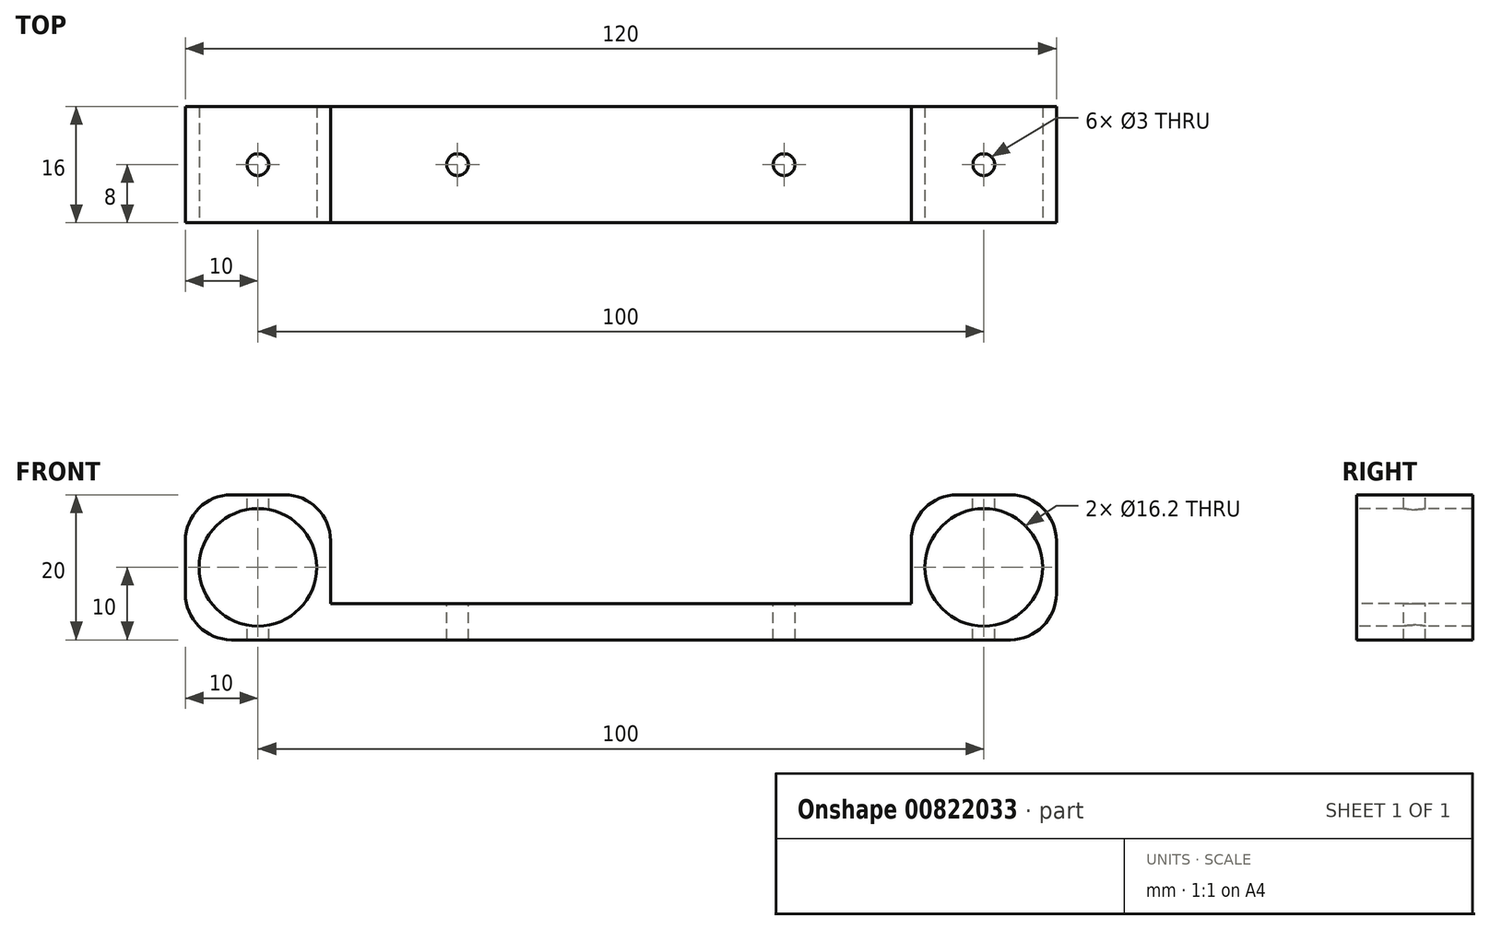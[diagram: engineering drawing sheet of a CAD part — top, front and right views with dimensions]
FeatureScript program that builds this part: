
annotation { "Feature Type Name" : "Feature", "Feature Type Description" : "" }
export const myFeature = defineFeature(function(context is Context, id is Id, definition is map)
    precondition{}
    {
        {
            var Q0;
            Q0=qCreatedBy(makeId("Top.planeOp"),FACE);
            var sketch = newSketch(context, id + "F0", { "sketchPlane" : qUnion([Q0])});
            skLineSegment(sketch, "E0.bottom", {"start": v(40, 8) * mm, "end": v(-40, 8) * mm});
            skLineSegment(sketch, "E0.top", {"start": v(40, -8) * mm, "end": v(-40, -8) * mm});
            skLineSegment(sketch, "E0.left", {"start": v(40, 8) * mm, "end": v(40, -8) * mm});
            skLineSegment(sketch, "E0.right", {"start": v(-40, 8) * mm, "end": v(-40, -8) * mm});
            skPoint(sketch, "E0.middle", {"position": v(0, 0) * mm});
            skLineSegment(sketch, "E1", {"start": v(40, -8) * mm, "end": v(40, 0) * mm});
            skLineSegment(sketch, "E2", {"start": v(-40, -8) * mm, "end": v(-40, 0) * mm});
            skSolve(sketch);
        }
        {
            var Q0;
            Q0=makeQuery(id+"F0.imprint","IMPRINT",FACE,{"disambiguationData":[TD([[makeQuery(id+"F0.imprint","IMPRINT",EDGE,{"derivedFrom":sQuery(id+"F0.wireOp",EDGE,"E0.bottom")}),1.0]])]});
            extrude(context, id + "F1", {"entities" : qUnion([Q0]), "depth" : 5 * mm, "offsetDistance" : 25.4 * mm});
        }
        {
            var Q0;
            Q0=makeQuery(id+"F1.opExtrude","SWEPT_FACE",FACE,{"disambiguationData":[OSD([sQuery(id+"F0.wireOp",EDGE,"E0.left"),sQuery(id+"F0.wireOp",EDGE,"E1")])]});
            var sketch = newSketch(context, id + "F2", { "sketchPlane" : qUnion([Q0])});
            skLineSegment(sketch, "E3.bottom", {"start": v(-8, 0) * mm, "end": v(8, 0) * mm});
            skLineSegment(sketch, "E3.right", {"start": v(8, 0) * mm, "end": v(8, -16) * mm});
            skLineSegment(sketch, "E4", {"start": v(-8, 0) * mm, "end": v(8, -16) * mm});
            skSolve(sketch);
        }
        {
            var Q0;
            Q0 = qSketchRegion(id + "F2", true);
            extrude(context, id + "F3", {"entities" : qUnion([Q0]), "operationType" : NewBodyOperationType.ADD, "oppositeDirection" : true, "depth" : 80 * mm, "offsetDistance" : 25.4 * mm});
        }
        {
            var Q0;
            Q0=makeQuery(id+"F3.boolean.opBoolean","MERGE",FACE,{"derivedFrom":[makeQuery(id+"F1.opExtrude","SWEPT_FACE",FACE,{"disambiguationData":[OSD([sQuery(id+"F0.wireOp",EDGE,"E0.left"),sQuery(id+"F0.wireOp",EDGE,"E1")])]}),makeQuery(id+"F3.opExtrude","CAP_FACE",FACE,{"disambiguationData":[OSD([sQuery(id+"F2.wireOp",EDGE,"E3.bottom"),sQuery(id+"F2.wireOp",EDGE,"E3.right"),sQuery(id+"F2.wireOp",EDGE,"E4")])],"isStart":true})]});
            var sketch = newSketch(context, id + "F4", { "sketchPlane" : qUnion([Q0])});
            skLineSegment(sketch, "E5.bottom", {"start": v(-8, 5) * mm, "end": v(8, 5) * mm});
            skLineSegment(sketch, "E5.top", {"start": v(-8, 0) * mm, "end": v(8, 0) * mm});
            skLineSegment(sketch, "E5.left", {"start": v(-8, 5) * mm, "end": v(-8, 0) * mm});
            skLineSegment(sketch, "E5.right", {"start": v(8, 5) * mm, "end": v(8, 0) * mm});
            skLineSegment(sketch, "E6.top", {"start": v(-8, 20) * mm, "end": v(8, 20) * mm});
            skLineSegment(sketch, "E6.left", {"start": v(-8, 0) * mm, "end": v(-8, 20) * mm});
            skLineSegment(sketch, "E6.right", {"start": v(8, 0) * mm, "end": v(8, 20) * mm});
            skSolve(sketch);
        }
        {
            var Q0;
            Q0 = qSketchRegion(id + "F4", true);
            extrude(context, id + "F5", {"entities" : qUnion([Q0]), "operationType" : NewBodyOperationType.ADD, "depth" : 20 * mm, "offsetDistance" : 25.4 * mm});
        }
        {
            var Q0;
            Q0=makeQuery(id+"F5.boolean.opBoolean","MERGE",FACE,{"derivedFrom":[makeQuery(id+"F1.opExtrude","SWEPT_FACE",FACE,{"disambiguationData":[OSD([sQuery(id+"F0.wireOp",EDGE,"E0.top")])]}),makeQuery(id+"F5.opExtrude","SWEPT_FACE",FACE,{"disambiguationData":[OSD([sQuery(id+"F4.wireOp",EDGE,"E6.left")])]})]});
            var sketch = newSketch(context, id + "F6", { "sketchPlane" : qUnion([Q0])});
            skLineSegment(sketch, "E7", {"start": v(60, 0) * mm, "end": v(40, 20) * mm});
            skLineSegment(sketch, "E8", {"start": v(60, 0) * mm, "end": v(50, 10) * mm});
            skCircle(sketch, "E9", {"center": v(50, 10) * mm, "radius": 8.1 * mm});
            skSolve(sketch);
        }
        {
            var Q0;
            Q0=makeQuery(id+"F3.boolean.opBoolean","MERGE",FACE,{"derivedFrom":[makeQuery(id+"F1.opExtrude","SWEPT_FACE",FACE,{"disambiguationData":[OSD([sQuery(id+"F0.wireOp",EDGE,"E0.right"),sQuery(id+"F0.wireOp",EDGE,"E2")])]}),makeQuery(id+"F3.opExtrude","CAP_FACE",FACE,{"disambiguationData":[OSD([sQuery(id+"F2.wireOp",EDGE,"E3.bottom"),sQuery(id+"F2.wireOp",EDGE,"E3.right"),sQuery(id+"F2.wireOp",EDGE,"E4")])],"isStart":false})]});
            var sketch = newSketch(context, id + "F7", { "sketchPlane" : qUnion([Q0])});
            skLineSegment(sketch, "E10.bottom", {"start": v(8, 0) * mm, "end": v(-8, 0) * mm});
            skLineSegment(sketch, "E10.top", {"start": v(8, 5) * mm, "end": v(-8, 5) * mm});
            skLineSegment(sketch, "E10.left", {"start": v(8, 0) * mm, "end": v(8, 5) * mm});
            skLineSegment(sketch, "E10.right", {"start": v(-8, 0) * mm, "end": v(-8, 5) * mm});
            skLineSegment(sketch, "E11.top", {"start": v(8, 20) * mm, "end": v(-8, 20) * mm});
            skLineSegment(sketch, "E11.left", {"start": v(8, 0) * mm, "end": v(8, 20) * mm});
            skLineSegment(sketch, "E11.right", {"start": v(-8, 0) * mm, "end": v(-8, 20) * mm});
            skSolve(sketch);
        }
        {
            var Q0;
            {var subQ0=sQuery(id+"F7.wireOp",EDGE,"E10.top");Q0=makeQuery(id+"F7.imprint","IMPRINT",FACE,{"disambiguationData":[TD([[makeQuery(id+"F7.imprint","IMPRINT",EDGE,{"derivedFrom":subQ0}),1.0]])]});}
            var Q1;
            {var subQ0=sQuery(id+"F7.wireOp",EDGE,"E10.top");Q1=makeQuery(id+"F7.imprint","IMPRINT",FACE,{"disambiguationData":[TD([[makeQuery(id+"F7.imprint","IMPRINT",EDGE,{"derivedFrom":subQ0}),-1.0]])]});}
            extrude(context, id + "F8", {"entities" : qUnion([Q0, Q1]), "operationType" : NewBodyOperationType.ADD, "depth" : 20 * mm, "offsetDistance" : 25.4 * mm});
        }
        {
            var Q0;
            Q0=makeQuery(id+"F8.boolean.opBoolean","MERGE",FACE,{"derivedFrom":[makeQuery(id+"F5.boolean.opBoolean","MERGE",FACE,{"derivedFrom":[makeQuery(id+"F1.opExtrude","SWEPT_FACE",FACE,{"disambiguationData":[OSD([sQuery(id+"F0.wireOp",EDGE,"E0.top")])]}),makeQuery(id+"F5.opExtrude","SWEPT_FACE",FACE,{"disambiguationData":[OSD([sQuery(id+"F4.wireOp",EDGE,"E6.left")])]})]}),makeQuery(id+"F8.opExtrude","SWEPT_FACE",FACE,{"disambiguationData":[OSD([sQuery(id+"F7.wireOp",EDGE,"E11.left")])]})]});
            var sketch = newSketch(context, id + "F9", { "sketchPlane" : qUnion([Q0])});
            skLineSegment(sketch, "E12", {"start": v(-60, 0) * mm, "end": v(-40, 20) * mm});
            skLineSegment(sketch, "E13", {"start": v(-40, 20) * mm, "end": v(-50, 10) * mm});
            skCircle(sketch, "E14", {"center": v(-50, 10) * mm, "radius": 8.1 * mm});
            skSolve(sketch);
        }
        {
            var Q0;
            {var subQ0=sQuery(id+"F9.wireOp",EDGE,"E13");var subQ1=sQuery(id+"F9.wireOp",EDGE,"E12");var subQ2=makeQuery(id+"F9.imprint","INTERSECT",VERTEX,{"derivedFrom":[subQ1,subQ0]});Q0=makeQuery(id+"F9.imprint","IMPRINT",FACE,{"disambiguationData":[TD([[makeQuery(id+"F9.imprint","IMPRINT",EDGE,{"disambiguationData":[TD([[subQ2,1.0]])],"derivedFrom":subQ1}),1.0]])]});}
            var Q1;
            {var subQ0=sQuery(id+"F9.wireOp",EDGE,"E13");var subQ1=sQuery(id+"F9.wireOp",EDGE,"E12");var subQ2=makeQuery(id+"F9.imprint","INTERSECT",VERTEX,{"derivedFrom":[subQ1,subQ0]});Q1=makeQuery(id+"F9.imprint","IMPRINT",FACE,{"disambiguationData":[TD([[makeQuery(id+"F9.imprint","IMPRINT",EDGE,{"disambiguationData":[TD([[subQ2,1.0]])],"derivedFrom":subQ1}),-1.0]])]});}
            var Q2;
            {var subQ0=sQuery(id+"F6.wireOp",EDGE,"E8");var subQ1=sQuery(id+"F6.wireOp",EDGE,"E7");var subQ2=makeQuery(id+"F6.imprint","INTERSECT",VERTEX,{"derivedFrom":[subQ1,subQ0]});Q2=makeQuery(id+"F6.imprint","IMPRINT",FACE,{"disambiguationData":[TD([[makeQuery(id+"F6.imprint","IMPRINT",EDGE,{"disambiguationData":[TD([[subQ2,-1.0]])],"derivedFrom":subQ1}),1.0]])]});}
            var Q3;
            {var subQ0=sQuery(id+"F6.wireOp",EDGE,"E8");var subQ1=sQuery(id+"F6.wireOp",EDGE,"E7");var subQ2=makeQuery(id+"F6.imprint","INTERSECT",VERTEX,{"derivedFrom":[subQ1,subQ0]});Q3=makeQuery(id+"F6.imprint","IMPRINT",FACE,{"disambiguationData":[TD([[makeQuery(id+"F6.imprint","IMPRINT",EDGE,{"disambiguationData":[TD([[subQ2,-1.0]])],"derivedFrom":subQ1}),-1.0]])]});}
            extrude(context, id + "F10", {"entities" : qUnion([Q0, Q1, Q2, Q3]), "operationType" : NewBodyOperationType.REMOVE, "oppositeDirection" : true, "depth" : 16 * mm, "offsetDistance" : 25.4 * mm});
        }
        {
            var Q0;
            Q0=makeQuery(id+"F5.opExtrude","CAP_EDGE",EDGE,{"disambiguationData":[OSD([sQuery(id+"F4.wireOp",EDGE,"E6.top")])],"isStart":true});
            var Q1;
            Q1=makeQuery(id+"F5.opExtrude","CAP_EDGE",EDGE,{"disambiguationData":[OSD([sQuery(id+"F4.wireOp",EDGE,"E6.top")])],"isStart":false});
            var Q2;
            Q2=makeQuery(id+"F5.opExtrude","CAP_EDGE",EDGE,{"disambiguationData":[OSD([sQuery(id+"F4.wireOp",EDGE,"E5.top")])],"isStart":false});
            var Q3;
            Q3=makeQuery(id+"F8.opExtrude","CAP_EDGE",EDGE,{"disambiguationData":[OSD([sQuery(id+"F7.wireOp",EDGE,"E10.bottom")])],"isStart":false});
            var Q4;
            Q4=makeQuery(id+"F8.opExtrude","CAP_EDGE",EDGE,{"disambiguationData":[OSD([sQuery(id+"F7.wireOp",EDGE,"E11.top")])],"isStart":false});
            var Q5;
            Q5=makeQuery(id+"F8.opExtrude","CAP_EDGE",EDGE,{"disambiguationData":[OSD([sQuery(id+"F7.wireOp",EDGE,"E11.top")])],"isStart":true});
            fillet(context, id + "F11", {"entities" : qUnion([Q0, Q1, Q2, Q3, Q4, Q5]), "radius" : 6.35 * mm, "tangentPropagation" : true, "allowEdgeOverflow" : false});
        }
        {
            var Q0;
            Q0=makeQuery(id+"F3.boolean.opBoolean","MERGE",FACE,{"derivedFrom":[makeQuery(id+"F1.opExtrude","SWEPT_FACE",FACE,{"disambiguationData":[OSD([sQuery(id+"F0.wireOp",EDGE,"E0.left"),sQuery(id+"F0.wireOp",EDGE,"E1")])]}),makeQuery(id+"F3.opExtrude","CAP_FACE",FACE,{"disambiguationData":[OSD([sQuery(id+"F2.wireOp",EDGE,"E3.bottom"),sQuery(id+"F2.wireOp",EDGE,"E3.right"),sQuery(id+"F2.wireOp",EDGE,"E4")])],"isStart":true})]});
            var sketch = newSketch(context, id + "F12", { "sketchPlane" : qUnion([Q0])});
            skLineSegment(sketch, "E15.bottom", {"start": v(8, 0) * mm, "end": v(-13.11, 0) * mm});
            skLineSegment(sketch, "E15.top", {"start": v(8, -25.45) * mm, "end": v(-13.11, -25.45) * mm});
            skLineSegment(sketch, "E15.left", {"start": v(8, 0) * mm, "end": v(8, -25.45) * mm});
            skLineSegment(sketch, "E15.right", {"start": v(-13.11, 0) * mm, "end": v(-13.11, -25.45) * mm});
            skSolve(sketch);
        }
        {
            var Q0;
            {var subQ1=makeQuery(id+"F3.opExtrude","CAP_EDGE",EDGE,{"disambiguationData":[OSD([sQuery(id+"F2.wireOp",EDGE,"E4")])],"isStart":true});Q0=makeQuery(id+"F12.imprint","IMPRINT",FACE,{"disambiguationData":[TD([[makeQuery(id+"F12.imprint","IMPRINT",EDGE,{"derivedFrom":subQ1}),1.0]])]});}
            extrude(context, id + "F13", {"entities" : qUnion([Q0]), "operationType" : NewBodyOperationType.REMOVE, "oppositeDirection" : true, "depth" : 80 * mm, "offsetDistance" : 25.4 * mm});
        }
        {
            var Q0;
            Q0=makeQuery(id+"F8.opExtrude","SWEPT_FACE",FACE,{"disambiguationData":[OSD([sQuery(id+"F7.wireOp",EDGE,"E11.top")])]});
            var sketch = newSketch(context, id + "F14", { "sketchPlane" : qUnion([Q0])});
            skLineSegment(sketch, "E16", {"start": v(-53.65, -8) * mm, "end": v(-46.35, 8) * mm});
            skLineSegment(sketch, "E17", {"start": v(-46.35, 8) * mm, "end": v(-50, 0) * mm});
            skCircle(sketch, "E18", {"center": v(-50, 0) * mm, "radius": 1.5 * mm});
            skSolve(sketch);
        }
        {
            var Q0;
            Q0=makeQuery(id+"F5.opExtrude","SWEPT_FACE",FACE,{"disambiguationData":[OSD([sQuery(id+"F4.wireOp",EDGE,"E6.top")])]});
            var sketch = newSketch(context, id + "F15", { "sketchPlane" : qUnion([Q0])});
            skLineSegment(sketch, "E19", {"start": v(46.35, -8) * mm, "end": v(53.65, 8) * mm});
            skLineSegment(sketch, "E20", {"start": v(53.65, 8) * mm, "end": v(50, 0) * mm});
            skCircle(sketch, "E21", {"center": v(50, 0) * mm, "radius": 1.5 * mm});
            skSolve(sketch);
        }
        {
            var Q0;
            {var subQ0=sQuery(id+"F14.wireOp",EDGE,"E17");var subQ1=sQuery(id+"F14.wireOp",EDGE,"E16");var subQ2=makeQuery(id+"F14.imprint","INTERSECT",VERTEX,{"derivedFrom":[subQ1,subQ0]});Q0=makeQuery(id+"F14.imprint","IMPRINT",FACE,{"disambiguationData":[TD([[makeQuery(id+"F14.imprint","IMPRINT",EDGE,{"disambiguationData":[TD([[subQ2,1.0]])],"derivedFrom":subQ1}),-1.0]])]});}
            var Q1;
            {var subQ0=sQuery(id+"F14.wireOp",EDGE,"E17");var subQ1=sQuery(id+"F14.wireOp",EDGE,"E16");var subQ2=makeQuery(id+"F14.imprint","INTERSECT",VERTEX,{"derivedFrom":[subQ1,subQ0]});Q1=makeQuery(id+"F14.imprint","IMPRINT",FACE,{"disambiguationData":[TD([[makeQuery(id+"F14.imprint","IMPRINT",EDGE,{"disambiguationData":[TD([[subQ2,1.0]])],"derivedFrom":subQ1}),1.0]])]});}
            var Q2;
            {var subQ0=sQuery(id+"F15.wireOp",EDGE,"E20");var subQ1=sQuery(id+"F15.wireOp",EDGE,"E19");var subQ2=makeQuery(id+"F15.imprint","INTERSECT",VERTEX,{"derivedFrom":[subQ1,subQ0]});Q2=makeQuery(id+"F15.imprint","IMPRINT",FACE,{"disambiguationData":[TD([[makeQuery(id+"F15.imprint","IMPRINT",EDGE,{"disambiguationData":[TD([[subQ2,1.0]])],"derivedFrom":subQ1}),-1.0]])]});}
            var Q3;
            {var subQ0=sQuery(id+"F15.wireOp",EDGE,"E20");var subQ1=sQuery(id+"F15.wireOp",EDGE,"E19");var subQ2=makeQuery(id+"F15.imprint","INTERSECT",VERTEX,{"derivedFrom":[subQ1,subQ0]});Q3=makeQuery(id+"F15.imprint","IMPRINT",FACE,{"disambiguationData":[TD([[makeQuery(id+"F15.imprint","IMPRINT",EDGE,{"disambiguationData":[TD([[subQ2,1.0]])],"derivedFrom":subQ1}),1.0]])]});}
            extrude(context, id + "F16", {"entities" : qUnion([Q0, Q1, Q2, Q3]), "operationType" : NewBodyOperationType.REMOVE, "oppositeDirection" : true, "depth" : 20 * mm, "offsetDistance" : 25.4 * mm});
        }
        {
            var Q0;
            Q0=makeQuery(id+"F1.opExtrude","CAP_FACE",FACE,{"disambiguationData":[OSD([sQuery(id+"F0.wireOp",EDGE,"E0.bottom"),sQuery(id+"F0.wireOp",EDGE,"E0.top"),sQuery(id+"F0.wireOp",EDGE,"E0.left"),sQuery(id+"F0.wireOp",EDGE,"E0.right"),sQuery(id+"F0.wireOp",EDGE,"E1"),sQuery(id+"F0.wireOp",EDGE,"E2")])],"isStart":false});
            var sketch = newSketch(context, id + "F17", { "sketchPlane" : qUnion([Q0])});
            skLineSegment(sketch, "E22", {"start": v(-40, 0) * mm, "end": v(-22.5, 0) * mm});
            skLineSegment(sketch, "E23", {"start": v(-22.5, 0) * mm, "end": v(22.5, 0) * mm});
            skLineSegment(sketch, "E24", {"start": v(22.5, 0) * mm, "end": v(40, 0) * mm});
            skCircle(sketch, "E25", {"center": v(-22.5, 0) * mm, "radius": 1.5 * mm});
            skCircle(sketch, "E26", {"center": v(22.5, 0) * mm, "radius": 1.5 * mm});
            skSolve(sketch);
        }
        {
            var Q0;
            {var subQ0=sQuery(id+"F17.wireOp",EDGE,"E23");var subQ1=sQuery(id+"F17.wireOp",EDGE,"E22");var subQ2=makeQuery(id+"F17.imprint","INTERSECT",VERTEX,{"derivedFrom":[subQ1,subQ0]});Q0=makeQuery(id+"F17.imprint","IMPRINT",FACE,{"disambiguationData":[TD([[makeQuery(id+"F17.imprint","IMPRINT",EDGE,{"disambiguationData":[TD([[subQ2,1.0]])],"derivedFrom":subQ1}),-1.0]])]});}
            var Q1;
            {var subQ0=sQuery(id+"F17.wireOp",EDGE,"E23");var subQ1=sQuery(id+"F17.wireOp",EDGE,"E22");var subQ2=makeQuery(id+"F17.imprint","INTERSECT",VERTEX,{"derivedFrom":[subQ1,subQ0]});Q1=makeQuery(id+"F17.imprint","IMPRINT",FACE,{"disambiguationData":[TD([[makeQuery(id+"F17.imprint","IMPRINT",EDGE,{"disambiguationData":[TD([[subQ2,1.0]])],"derivedFrom":subQ1}),1.0]])]});}
            var Q2;
            {var subQ0=sQuery(id+"F17.wireOp",EDGE,"E24");var subQ1=sQuery(id+"F17.wireOp",EDGE,"E23");var subQ2=makeQuery(id+"F17.imprint","INTERSECT",VERTEX,{"derivedFrom":[subQ1,subQ0]});Q2=makeQuery(id+"F17.imprint","IMPRINT",FACE,{"disambiguationData":[TD([[makeQuery(id+"F17.imprint","IMPRINT",EDGE,{"disambiguationData":[TD([[subQ2,1.0]])],"derivedFrom":subQ1}),-1.0]])]});}
            var Q3;
            {var subQ0=sQuery(id+"F17.wireOp",EDGE,"E24");var subQ1=sQuery(id+"F17.wireOp",EDGE,"E23");var subQ2=makeQuery(id+"F17.imprint","INTERSECT",VERTEX,{"derivedFrom":[subQ1,subQ0]});Q3=makeQuery(id+"F17.imprint","IMPRINT",FACE,{"disambiguationData":[TD([[makeQuery(id+"F17.imprint","IMPRINT",EDGE,{"disambiguationData":[TD([[subQ2,1.0]])],"derivedFrom":subQ1}),1.0]])]});}
            extrude(context, id + "F18", {"entities" : qUnion([Q0, Q1, Q2, Q3]), "operationType" : NewBodyOperationType.REMOVE, "oppositeDirection" : true, "depth" : 10 * mm, "offsetDistance" : 25.4 * mm});
        }
    });
